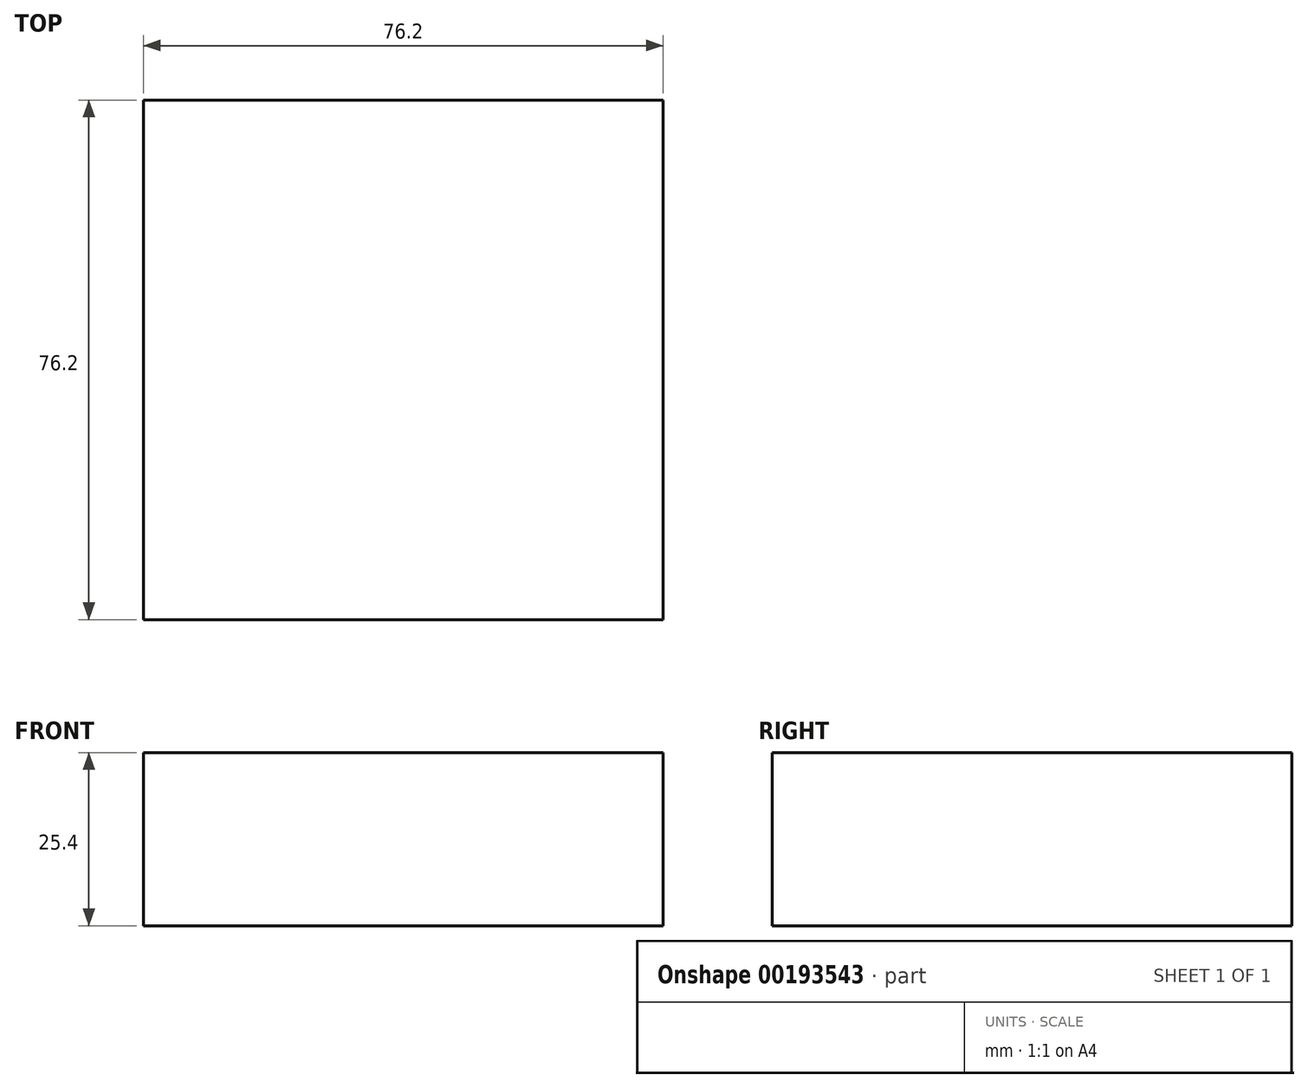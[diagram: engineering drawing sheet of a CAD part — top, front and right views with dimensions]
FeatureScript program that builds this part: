
annotation { "Feature Type Name" : "Feature", "Feature Type Description" : "" }
export const myFeature = defineFeature(function(context is Context, id is Id, definition is map)
    precondition{}
    {
        {
            var Q0;
            Q0=qCreatedBy(makeId("Top.planeOp"),FACE);
            var sketch = newSketch(context, id + "F0", { "sketchPlane" : qUnion([Q0])});
            skLineSegment(sketch, "E0.bottom", {"start": v(-11.03, 53.36) * mm, "end": v(-87.23, 53.36) * mm});
            skLineSegment(sketch, "E0.top", {"start": v(-11.03, -22.84) * mm, "end": v(-87.23, -22.84) * mm});
            skLineSegment(sketch, "E0.left", {"start": v(-11.03, 53.36) * mm, "end": v(-11.03, -22.84) * mm});
            skLineSegment(sketch, "E0.right", {"start": v(-87.23, 53.36) * mm, "end": v(-87.23, -22.84) * mm});
            skPoint(sketch, "E0.middle", {"position": v(-49.13, 15.26) * mm});
            skSolve(sketch);
        }
        {
            var Q0;
            Q0 = qSketchRegion(id + "F0", true);
            extrude(context, id + "F1", {"entities" : qUnion([Q0]), "depth" : 25.4 * mm});
        }
    });
